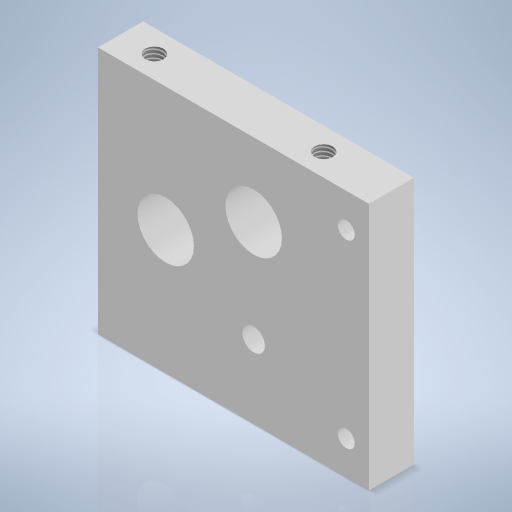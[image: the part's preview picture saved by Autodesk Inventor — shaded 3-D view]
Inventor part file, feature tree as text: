
AUTODESK INVENTOR PART (.ipt)
format: ipt  version: 2024 (Build 280153000, 153)  size: 258,560 bytes
history: native  units: mm
features: sketch x5, hole x3, extrude x2, plane x1, mirror x1
ambient origin geometry x8: Origin, YZ Plane, XZ Plane, XY Plane, X Axis, Y Axis, Z Axis, Center Point
bodies: Volumenkörper1 (feature_tree)
feature tree (12):
  extrude  "Extrusion1"  Depth=48.0mm
  extrude  "Extrusion2"  Depth=8.0mm
  hole  "Bohrung1"  [1 undecoded]
  hole  "Bohrung2"  [1 undecoded]
  hole  "Bohrung3"  [1 undecoded]
  plane  "Arbeitsebene1"
  mirror  "Spiegeln1"
  sketch  "Skizze1"  dims[d0=44.0mm d1=48.0mm]
  sketch  "Skizze2"  dims[d2=8.0mm d3=0.0mm d4=9.0mm]
  sketch  "Skizze3"  dims[d5=12.0mm d6=10.0mm]
  sketch  "Skizze4"  dims[d7=18.0mm d8=10.0mm]
  sketch  "Skizze5"  dims[d9=4.0mm d10=8.0mm d11=0.0mm d12=3.242mm d13=4.0mm d14=4.0mm d15=2.0mm d16=90.0deg d17=4.0mm d18=0.0mm d19=3.0mm d20=4.0mm d21=4.0mm d22=2.0mm d23=90.0deg d24=4.0mm d25=0.0mm d26=4.0mm d27=6.0mm d28=32.0mm d29=3.242mm d30=8.0mm d31=4.0mm d32=2.0mm d33=90.0deg d34=10.0mm d35=0.0mm d36=30.0mm d37=12.0mm d38=-22.0mm]
note: 3 required parameter values undecoded (feature->parameter linkage not recoverable at this tier; creation-order binding heuristic only, values carry confidence <= 0.55)
